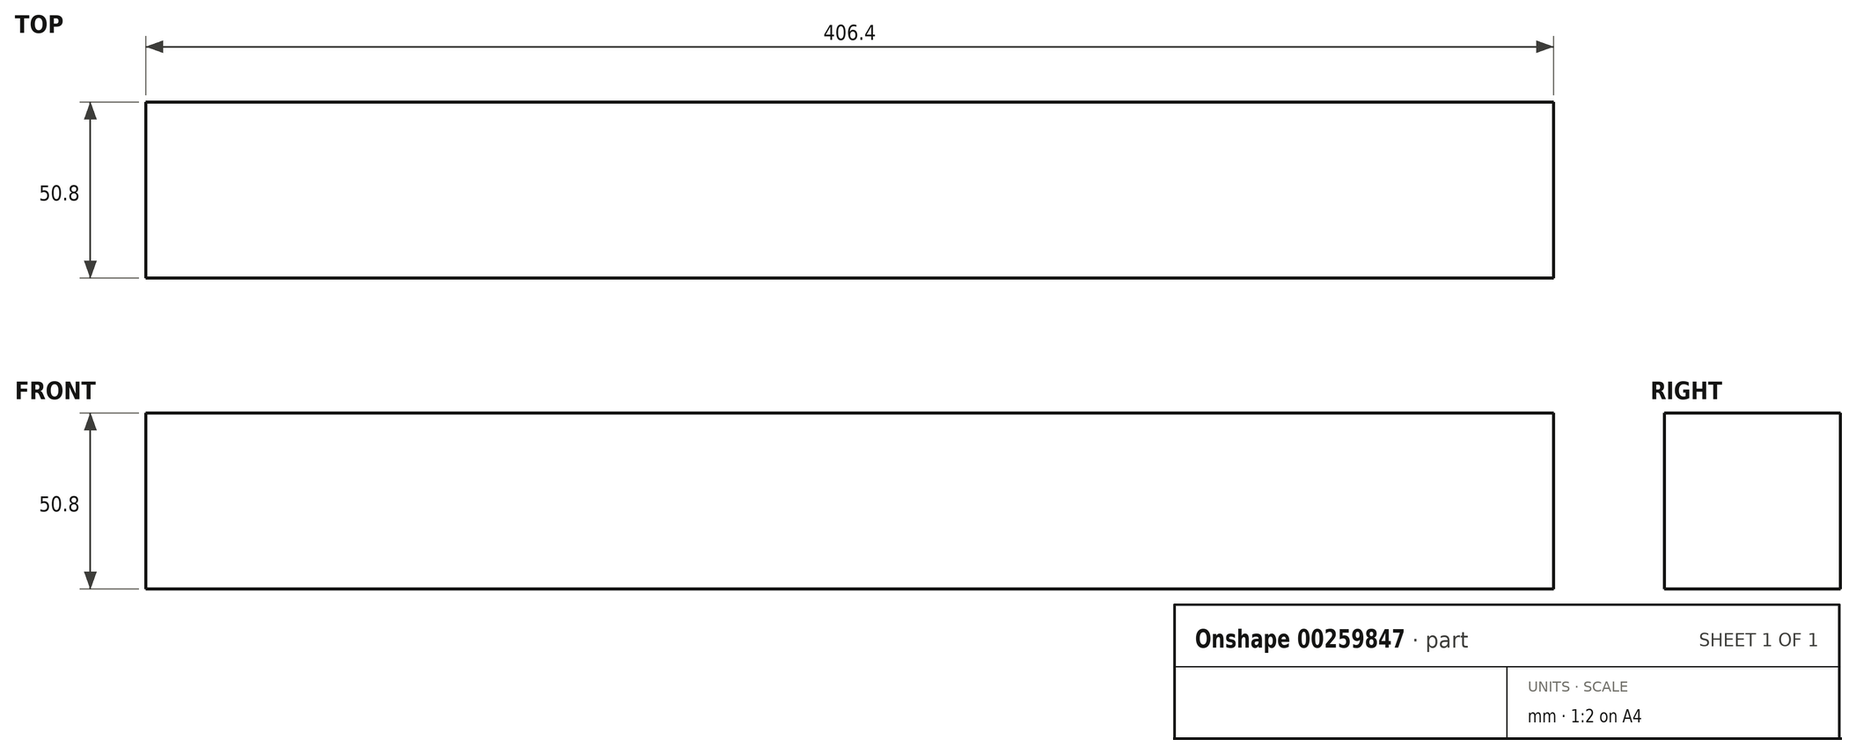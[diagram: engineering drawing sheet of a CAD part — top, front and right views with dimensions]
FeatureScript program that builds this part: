
annotation { "Feature Type Name" : "Feature", "Feature Type Description" : "" }
export const myFeature = defineFeature(function(context is Context, id is Id, definition is map)
    precondition{}
    {
        {
            var Q0;
            Q0=qCreatedBy(makeId("Right.planeOp"),FACE);
            var sketch = newSketch(context, id + "F0", { "sketchPlane" : qUnion([Q0])});
            skLineSegment(sketch, "E0.bottom", {"start": v(-25.4, 25.4) * mm, "end": v(25.4, 25.4) * mm});
            skLineSegment(sketch, "E0.top", {"start": v(-25.4, -25.4) * mm, "end": v(25.4, -25.4) * mm});
            skLineSegment(sketch, "E0.left", {"start": v(-25.4, 25.4) * mm, "end": v(-25.4, -25.4) * mm});
            skLineSegment(sketch, "E0.right", {"start": v(25.4, 25.4) * mm, "end": v(25.4, -25.4) * mm});
            skSolve(sketch);
        }
        {
            var Q0;
            Q0 = qSketchRegion(id + "F0", true);
            extrude(context, id + "F1", {"entities" : qUnion([Q0]), "depth" : 406.4 * mm});
        }
    });
